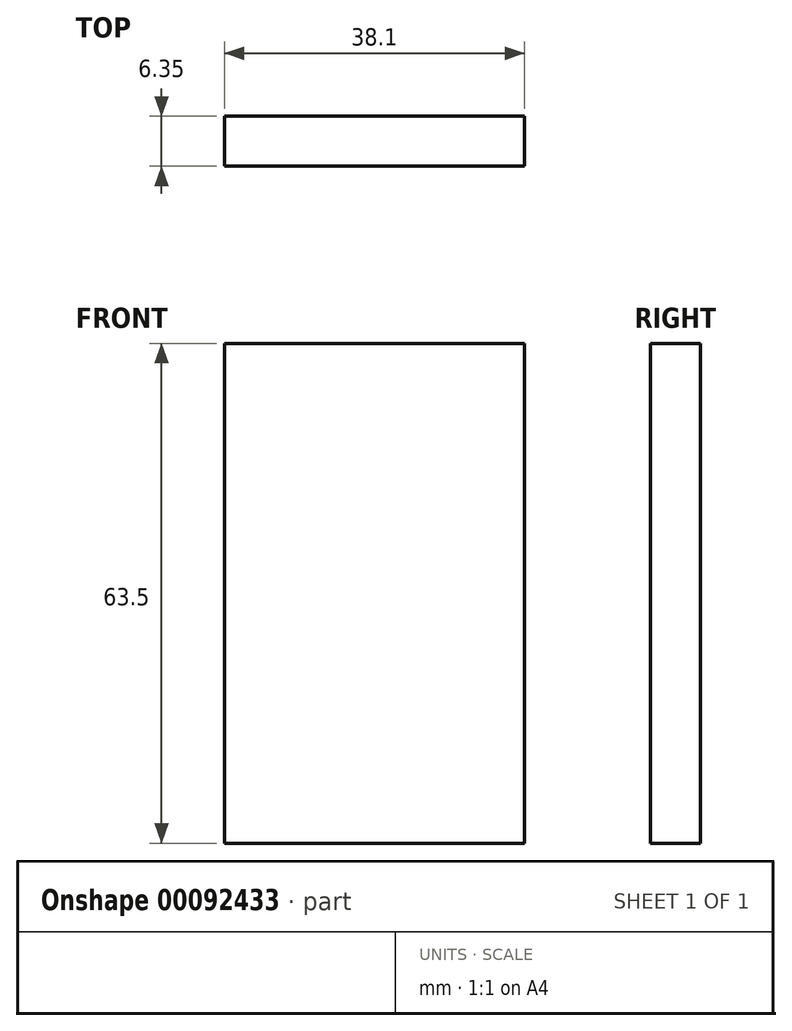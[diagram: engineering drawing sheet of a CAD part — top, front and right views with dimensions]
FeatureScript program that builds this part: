
annotation { "Feature Type Name" : "Feature", "Feature Type Description" : "" }
export const myFeature = defineFeature(function(context is Context, id is Id, definition is map)
    precondition{}
    {
        {
            var Q0;
            Q0=qCreatedBy(makeId("Front.planeOp"),FACE);
            var sketch = newSketch(context, id + "F0", { "sketchPlane" : qUnion([Q0])});
            skLineSegment(sketch, "E0.bottom", {"start": v(-20.99, 47.13) * mm, "end": v(17.11, 47.13) * mm});
            skLineSegment(sketch, "E0.top", {"start": v(-20.99, -16.37) * mm, "end": v(17.11, -16.37) * mm});
            skLineSegment(sketch, "E0.left", {"start": v(-20.99, 47.13) * mm, "end": v(-20.99, -16.37) * mm});
            skLineSegment(sketch, "E0.right", {"start": v(17.11, 47.13) * mm, "end": v(17.11, -16.37) * mm});
            skSolve(sketch);
        }
        {
            var Q0;
            Q0=makeQuery(id+"F0.imprint","IMPRINT",FACE,{"disambiguationData":[TD([[makeQuery(id+"F0.imprint","IMPRINT",EDGE,{"derivedFrom":sQuery(id+"F0.wireOp",EDGE,"E0.bottom")}),-1.0]])]});
            extrude(context, id + "F1", {"entities" : qUnion([Q0]), "depth" : 6.35 * mm});
        }
    });
